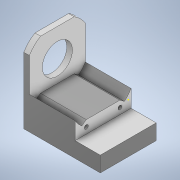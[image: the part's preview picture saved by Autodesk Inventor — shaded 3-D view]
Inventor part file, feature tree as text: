
AUTODESK INVENTOR PART (.ipt)
format: ipt  version: 2022 (Build 260153000, 153)  size: 1,077,248 bytes
history: mixed  units: mm
features: sketch x5, extrude x4, other x3, imported_body x1
ambient origin geometry x8: Origin, YZ Plane, XZ Plane, XY Plane, X Axis, Y Axis, Z Axis, Center Point
bodies: Solid1 (imported_parasolid)
feature tree (13):
  other  "Assembly2.iam"
  other  "96Gears_Stage_1_modified.ipt:1"
  other  "96Gears_Stage_2_modified.ipt:1"
  extrude  "Extrusion3"  Depth=10.0mm
  extrude  "Extrusion5"  Depth=6.0mm TaperAngle=0.0deg
  extrude  "Extrusion6"  Depth=6.0mm TaperAngle=0.0deg
  extrude  "Extrusion7"  Depth=10.0mm TaperAngle=0.0deg
  sketch  "Sketch5"  dims[d7=6.0mm d8=18.0mm d9=0.0mm]
  sketch  "Sketch4"  dims[d0=10.0mm d6=3.0mm]
  sketch  "Sketch7"  dims[d17=32.25mm d18=6.0mm d19=0.0mm]
  sketch  "Sketch8"  dims[d20=10.0mm d21=10.0mm d22=0.0mm]
  sketch  "Sketch9"  dims[d24=4.1mm d25=4.1mm d26=10.0mm d27=0.0mm]
  imported_body  NMx_Import_Brep_tag  [imported B-rep: ~21 faces, bbox_mm=[82.0, 83.027756, 60.0]]
